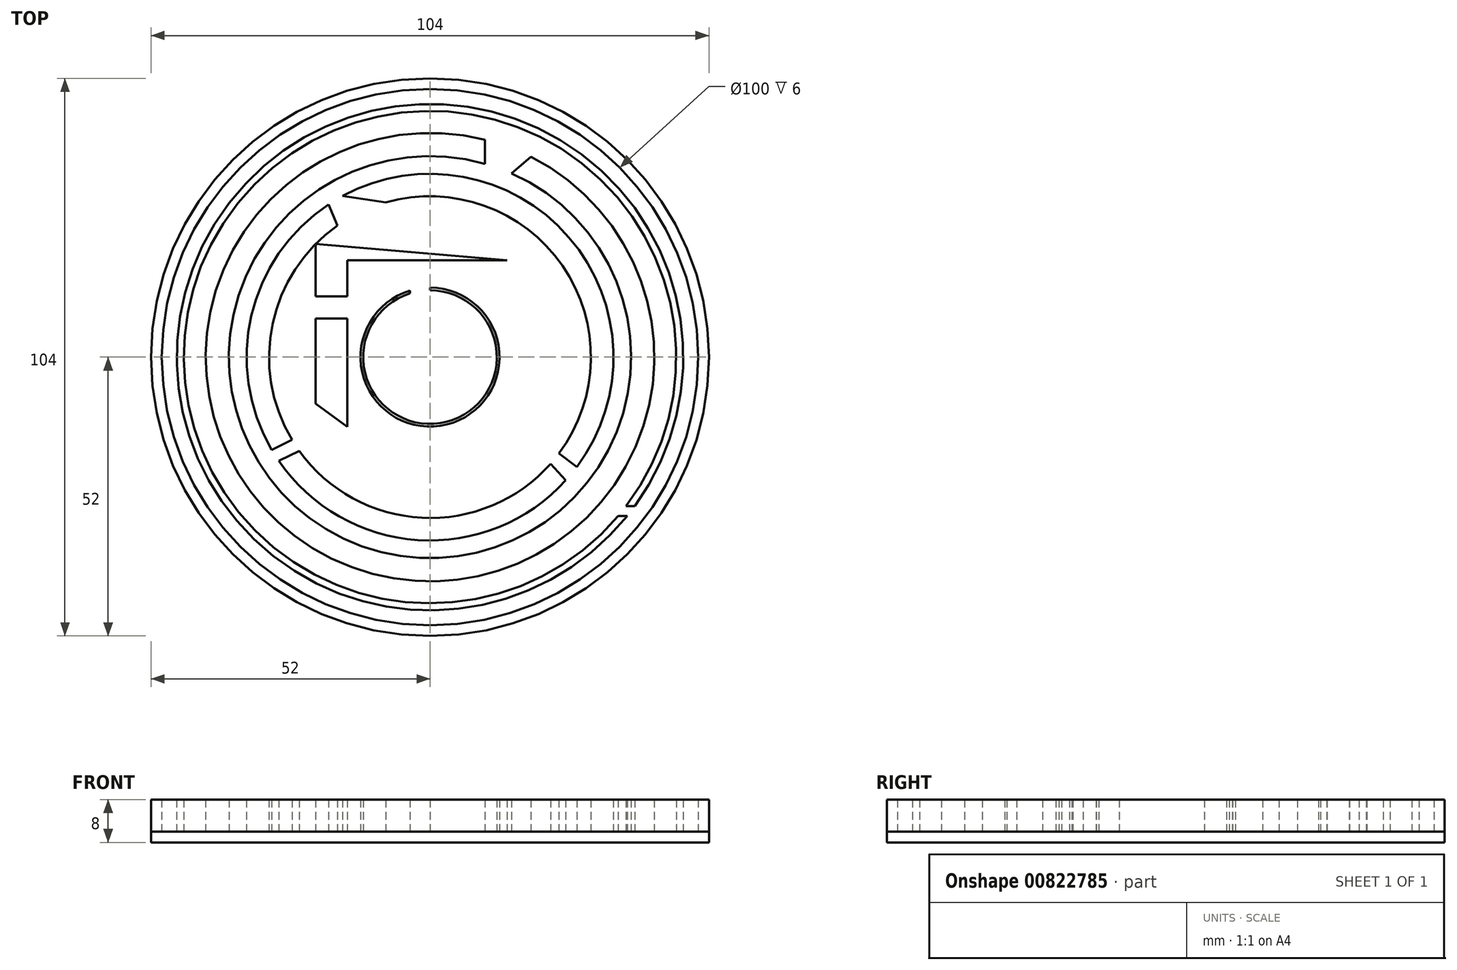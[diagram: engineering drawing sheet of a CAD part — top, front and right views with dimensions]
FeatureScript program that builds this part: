
annotation { "Feature Type Name" : "Feature", "Feature Type Description" : "" }
export const myFeature = defineFeature(function(context is Context, id is Id, definition is map)
    precondition{}
    {
        {
            var Q0;
            Q0=qCreatedBy(makeId("Top.planeOp"),FACE);
            var sketch = newSketch(context, id + "F0", { "sketchPlane" : qUnion([Q0])});
            skCircle(sketch, "E0", {"center": v(0, 0) * mm, "radius": 50 * mm});
            skArc(sketch, "E1.0", {"start": v(-17.26, 24.53) * mm, "mid": v(-29.35, 6.22) * mm, "end": v(-25.73, -15.42) * mm});
            skArc(sketch, "E2", {"start": v(10.24, 40.53) * mm, "mid": v(-14.61, -39.17) * mm, "end": v(18.81, 37.33) * mm});
            skArc(sketch, "E3.0", {"start": v(38.16, -27.79) * mm, "mid": v(-37.47, 28.72) * mm, "end": v(36.75, -29.63) * mm});
            skArc(sketch, "E4.0", {"start": v(36.54, -27.79) * mm, "mid": v(-35.82, 28.72) * mm, "end": v(35.06, -29.63) * mm});
            skArc(sketch, "E5", {"start": v(10.24, 36.06) * mm, "mid": v(-12.74, -35.26) * mm, "end": v(15.18, 34.28) * mm});
            skArc(sketch, "E6.0", {"start": v(-18.9, 28.5) * mm, "mid": v(-33.3, 7.72) * mm, "end": v(-29.5, -17.28) * mm});
            skLineSegment(sketch, "E7", {"start": v(36.54, -27.79) * mm, "end": v(38.16, -27.79) * mm});
            skLineSegment(sketch, "E8", {"start": v(10.24, 40.53) * mm, "end": v(10.24, 36.06) * mm});
            skLineSegment(sketch, "E9", {"start": v(18.81, 37.33) * mm, "end": v(15.18, 34.28) * mm});
            skLineSegment(sketch, "E10", {"start": v(-18.9, 28.5) * mm, "end": v(-17.26, 24.53) * mm});
            skLineSegment(sketch, "E11", {"start": v(-16.29, 30.06) * mm, "end": v(-8.24, 28.84) * mm});
            skArc(sketch, "E12.trimOffspring", {"start": v(24.03, -17.96) * mm, "mid": v(24.7, 17.03) * mm, "end": v(-8.24, 28.84) * mm});
            skArc(sketch, "E13.trimOffspring", {"start": v(-24.37, -17.5) * mm, "mid": v(-1.53, -29.96) * mm, "end": v(22.46, -19.89) * mm});
            skPoint(sketch, "E14.end.orphan", {"position": v(0, 26.33) * mm});
            skPoint(sketch, "E15.start.orphan", {"position": v(0, -30) * mm});
            skLineSegment(sketch, "E16.bottom", {"start": v(-15.43, 18.08) * mm, "end": v(-8.18, 18.08) * mm});
            skLineSegment(sketch, "E16.left", {"start": v(-15.43, 18.08) * mm, "end": v(-15.43, 11.33) * mm});
            skLineSegment(sketch, "E17", {"start": v(-21.3, 21.12) * mm, "end": v(-8.18, 20) * mm});
            skLineSegment(sketch, "E18", {"start": v(-21.3, 21.12) * mm, "end": v(-21.3, 11.33) * mm});
            skLineSegment(sketch, "E19", {"start": v(-21.3, -8.68) * mm, "end": v(-15.43, -13) * mm});
            skLineSegment(sketch, "E20.trimOffspring", {"start": v(-0.9, 19.38) * mm, "end": v(14.34, 18.08) * mm});
            skLineSegment(sketch, "E21.trimOffspring", {"start": v(-0.9, 18.08) * mm, "end": v(14.34, 18.08) * mm});
            skArc(sketch, "E22", {"start": v(-3.77, 11.87) * mm, "mid": v(1.9, -12.3) * mm, "end": v(0, 12.45) * mm});
            skArc(sketch, "E23.0", {"start": v(-3.77, 12.4) * mm, "mid": v(1.9, -12.81) * mm, "end": v(0, 12.95) * mm});
            skPoint(sketch, "E24.orphan", {"position": v(0, 11.42) * mm});
            skLineSegment(sketch, "E25", {"start": v(-8.18, 18.08) * mm, "end": v(-0.55, 18.08) * mm});
            skLineSegment(sketch, "E26", {"start": v(-8.18, 20) * mm, "end": v(-0.9, 19.38) * mm});
            skLineSegment(sketch, "E27.top", {"start": v(-21.3, 7.23) * mm, "end": v(-15.43, 7.23) * mm});
            skLineSegment(sketch, "E28.trimOffspring", {"start": v(-21.3, 7.23) * mm, "end": v(-21.3, -8.68) * mm});
            skLineSegment(sketch, "E29.trimOffspring", {"start": v(-15.43, 7.23) * mm, "end": v(-15.43, -13) * mm});
            skLineSegment(sketch, "E30", {"start": v(-21.3, 11.33) * mm, "end": v(-15.43, 11.33) * mm});
            skCircle(sketch, "E31.0", {"center": v(0, 0) * mm, "radius": 52 * mm});
            skLineSegment(sketch, "E32", {"start": v(22.46, -19.89) * mm, "end": v(25.31, -22.98) * mm});
            skLineSegment(sketch, "E33", {"start": v(24.03, -17.96) * mm, "end": v(27.36, -20.5) * mm});
            skLineSegment(sketch, "E34", {"start": v(-25.73, -15.42) * mm, "end": v(-29.5, -17.28) * mm});
            skLineSegment(sketch, "E35", {"start": v(-24.37, -17.5) * mm, "end": v(-28.17, -19.37) * mm});
            skArc(sketch, "E36.trimOffspring", {"start": v(-28.17, -19.37) * mm, "mid": v(-2.3, -34.11) * mm, "end": v(25.31, -22.98) * mm});
            skArc(sketch, "E37.trimOffspring", {"start": v(27.36, -20.5) * mm, "mid": v(25.88, 22.34) * mm, "end": v(-16.29, 30.06) * mm});
            skLineSegment(sketch, "E38", {"start": v(-3.77, 12.4) * mm, "end": v(-3.77, 11.87) * mm});
            skLineSegment(sketch, "E39", {"start": v(0, 12.95) * mm, "end": v(0, 12.45) * mm});
            skLineSegment(sketch, "E40.bottom", {"start": v(35.24, -29.23) * mm, "end": v(35.4, -29.23) * mm});
            skLineSegment(sketch, "E40.top", {"start": v(35.06, -29.63) * mm, "end": v(36.75, -29.63) * mm});
            skPoint(sketch, "E40.left.start.orphan", {"position": v(34.8, -29.23) * mm});
            skSolve(sketch);
        }
        {
            var Q0;
            Q0=makeQuery(id+"F0.imprint","IMPRINT",FACE,{"disambiguationData":[TD([[makeQuery(id+"F0.imprint","IMPRINT",EDGE,{"derivedFrom":sQuery(id+"F0.wireOp",EDGE,"E0")}),-1.0]])]});
            var Q1;
            {var subQ0=sQuery(id+"F0.wireOp",EDGE,"E3.0");Q1=makeQuery(id+"F0.imprint","IMPRINT",FACE,{"disambiguationData":[TD([[makeQuery(id+"F0.imprint","IMPRINT",EDGE,{"derivedFrom":subQ0}),1.0]])]});}
            var Q2;
            Q2=makeQuery(id+"F0.imprint","IMPRINT",FACE,{"disambiguationData":[TD([[makeQuery(id+"F0.imprint","IMPRINT",EDGE,{"derivedFrom":sQuery(id+"F0.wireOp",EDGE,"E2")}),1.0]])]});
            var Q3;
            Q3=makeQuery(id+"F0.imprint","IMPRINT",FACE,{"disambiguationData":[TD([[makeQuery(id+"F0.imprint","IMPRINT",EDGE,{"derivedFrom":sQuery(id+"F0.wireOp",EDGE,"E13.trimOffspring")}),-1.0]])]});
            var Q4;
            Q4=makeQuery(id+"F0.imprint","IMPRINT",FACE,{"disambiguationData":[TD([[makeQuery(id+"F0.imprint","IMPRINT",EDGE,{"derivedFrom":sQuery(id+"F0.wireOp",EDGE,"E6.0")}),1.0]])]});
            var Q5;
            Q5=makeQuery(id+"F0.imprint","IMPRINT",FACE,{"disambiguationData":[TD([[makeQuery(id+"F0.imprint","IMPRINT",EDGE,{"derivedFrom":sQuery(id+"F0.wireOp",EDGE,"E11")}),1.0]])]});
            var Q6;
            {var subQ0=sQuery(id+"F0.wireOp",EDGE,"E16.bottom");Q6=makeQuery(id+"F0.imprint","IMPRINT",FACE,{"disambiguationData":[TD([[makeQuery(id+"F0.imprint","IMPRINT",EDGE,{"derivedFrom":subQ0}),1.0]])]});}
            var Q7;
            Q7=makeQuery(id+"F0.imprint","IMPRINT",FACE,{"disambiguationData":[TD([[makeQuery(id+"F0.imprint","IMPRINT",EDGE,{"derivedFrom":sQuery(id+"F0.wireOp",EDGE,"E19")}),1.0]])]});
            var Q8;
            Q8=makeQuery(id+"F0.imprint","IMPRINT",FACE,{"disambiguationData":[TD([[makeQuery(id+"F0.imprint","IMPRINT",EDGE,{"derivedFrom":sQuery(id+"F0.wireOp",EDGE,"E22")}),-1.0]])]});
            extrude(context, id + "F1", {"entities" : qUnion([Q0, Q1, Q2, Q3, Q4, Q5, Q6, Q7, Q8]), "depth" : 6 * mm, "offsetDistance" : 25 * mm});
        }
        {
            var Q0;
            Q0=qCreatedBy(makeId("Top.planeOp"),FACE);
            var sketch = newSketch(context, id + "F2", { "sketchPlane" : qUnion([Q0])});
            skCircle(sketch, "E41.0", {"center": v(0, 0) * mm, "radius": 52 * mm});
            skSolve(sketch);
        }
        {
            var Q0;
            Q0 = qSketchRegion(id + "F2", true);
            extrude(context, id + "F3", {"entities" : qUnion([Q0]), "oppositeDirection" : true, "depth" : 2 * mm, "offsetDistance" : 25 * mm});
        }
    });
